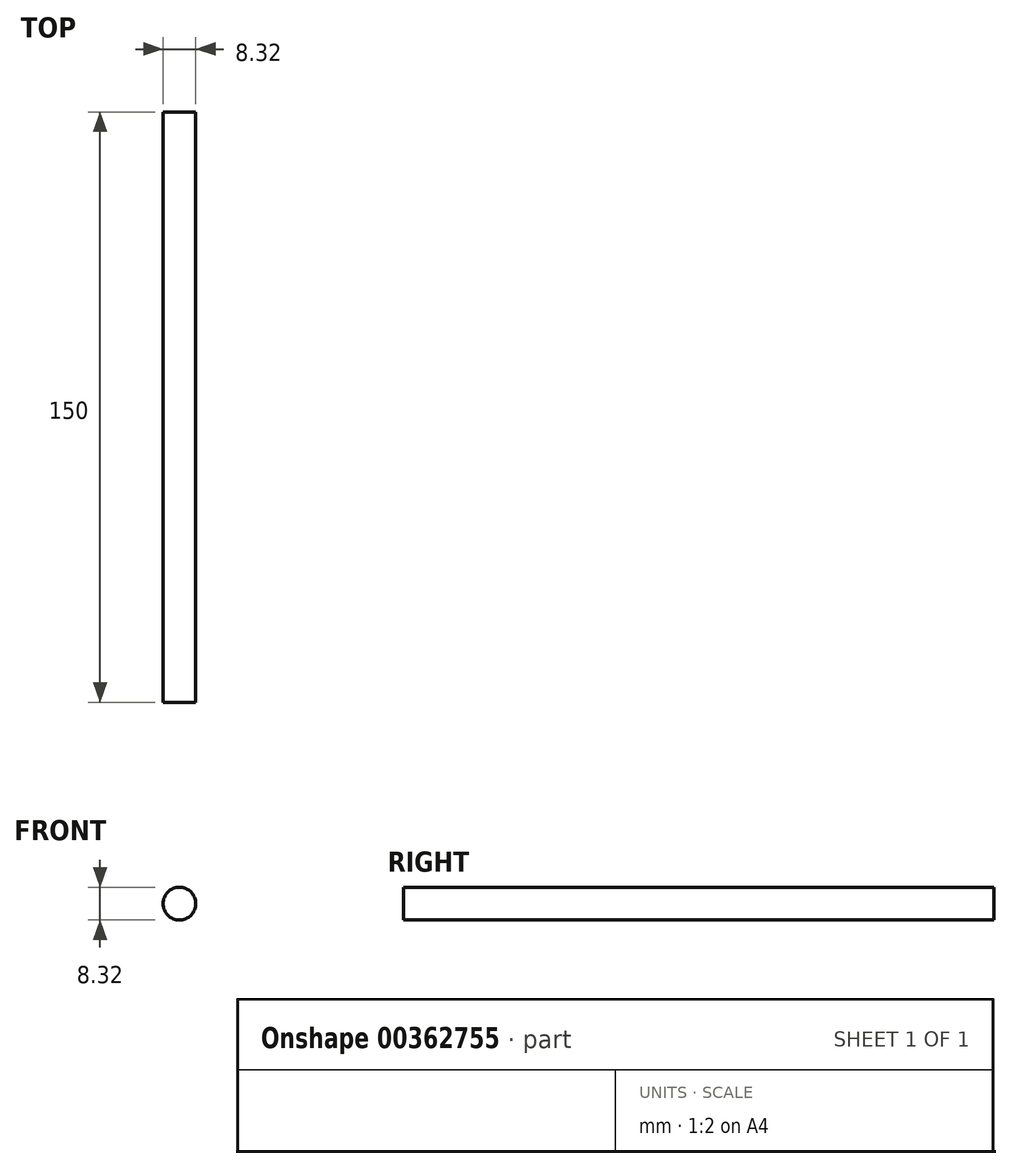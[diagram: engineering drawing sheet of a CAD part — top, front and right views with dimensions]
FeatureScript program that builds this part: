
annotation { "Feature Type Name" : "Feature", "Feature Type Description" : "" }
export const myFeature = defineFeature(function(context is Context, id is Id, definition is map)
    precondition{}
    {
        {
            var Q0;
            Q0=qCreatedBy(makeId("Front.planeOp"),FACE);
            var sketch = newSketch(context, id + "F0", { "sketchPlane" : qUnion([Q0])});
            skCircle(sketch, "E0", {"center": v(0, 0) * mm, "radius": 4.16 * mm});
            skSolve(sketch);
        }
        {
            var Q0;
            Q0=makeQuery(id+"F0.imprint","IMPRINT",FACE,{"disambiguationData":[TD([[makeQuery(id+"F0.imprint","IMPRINT",EDGE,{"derivedFrom":sQuery(id+"F0.wireOp",EDGE,"E0")}),1.0]])]});
            extrude(context, id + "F1", {"entities" : qUnion([Q0]), "depth" : 150 * mm});
        }
    });
